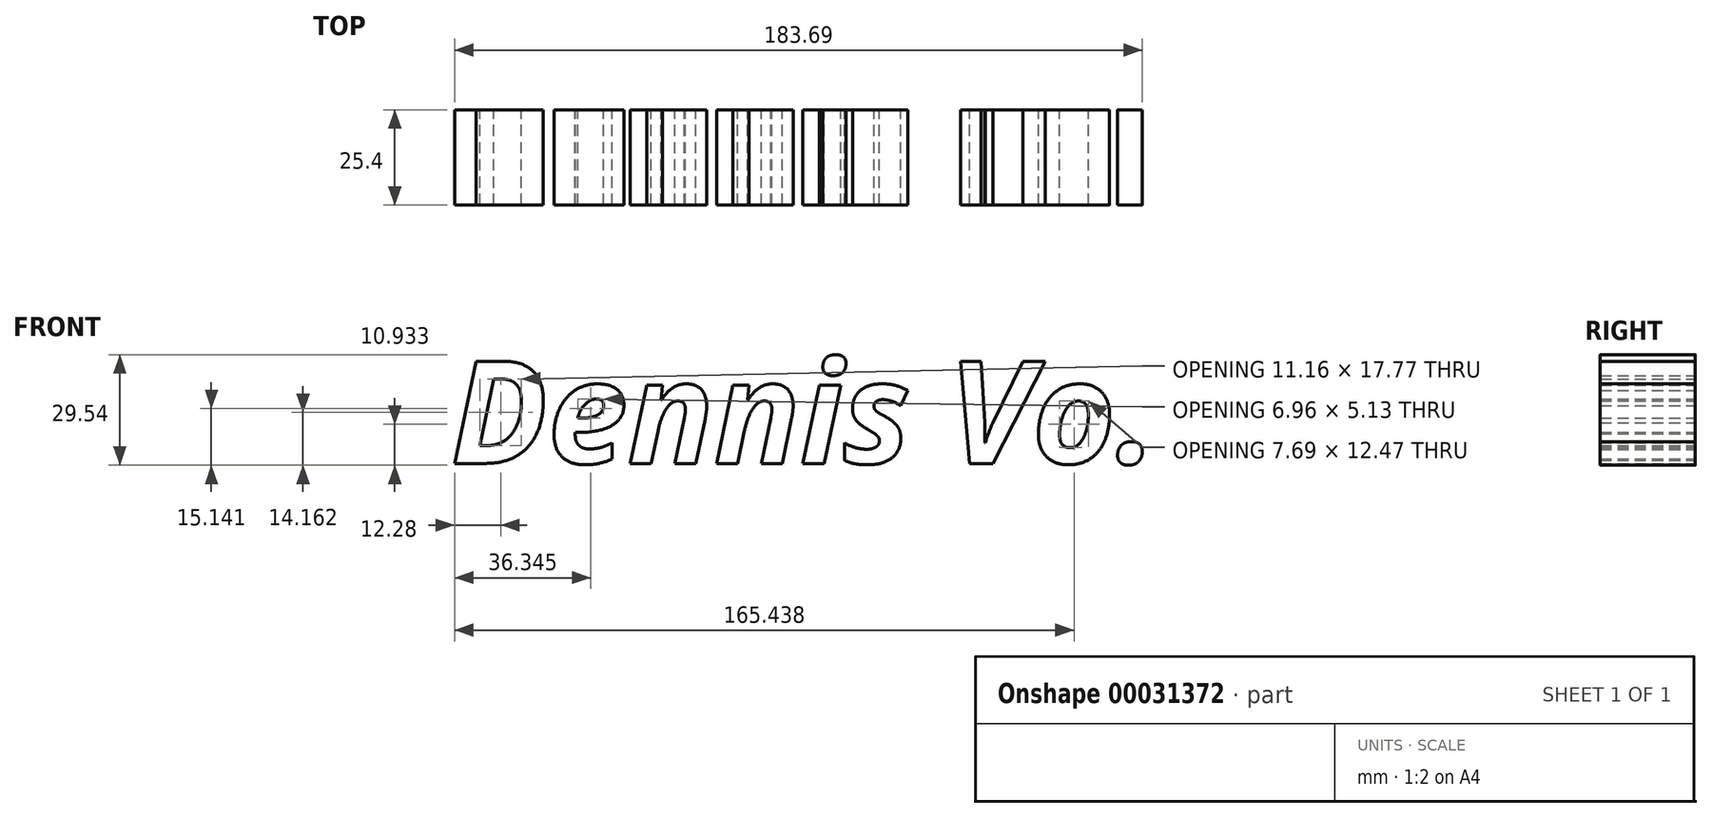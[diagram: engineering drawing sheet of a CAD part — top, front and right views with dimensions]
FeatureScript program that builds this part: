
annotation { "Feature Type Name" : "Feature", "Feature Type Description" : "" }
export const myFeature = defineFeature(function(context is Context, id is Id, definition is map)
    precondition{}
    {
        {
            var Q0;
            Q0=qCreatedBy(makeId("Front.planeOp"),FACE);
            var sketch = newSketch(context, id + "F0", { "sketchPlane" : qUnion([Q0])});
            skText(sketch, "E0", { "text": "Dennis Vo. ", "fontName": "OpenSans-BoldItalic.ttf"});
            const initialGuessF0  = {"E0": [-0.09187, -0.00845, 1, 0, 0.02752]};
            skSetInitialGuess(sketch, initialGuessF0);
            skSolve(sketch);
        }
        {
            var Q0;
            Q0 = qSketchRegion(id + "F0", true);
            extrude(context, id + "F1", {"entities" : qUnion([Q0]), "depth" : 25.4 * mm});
        }
    });
